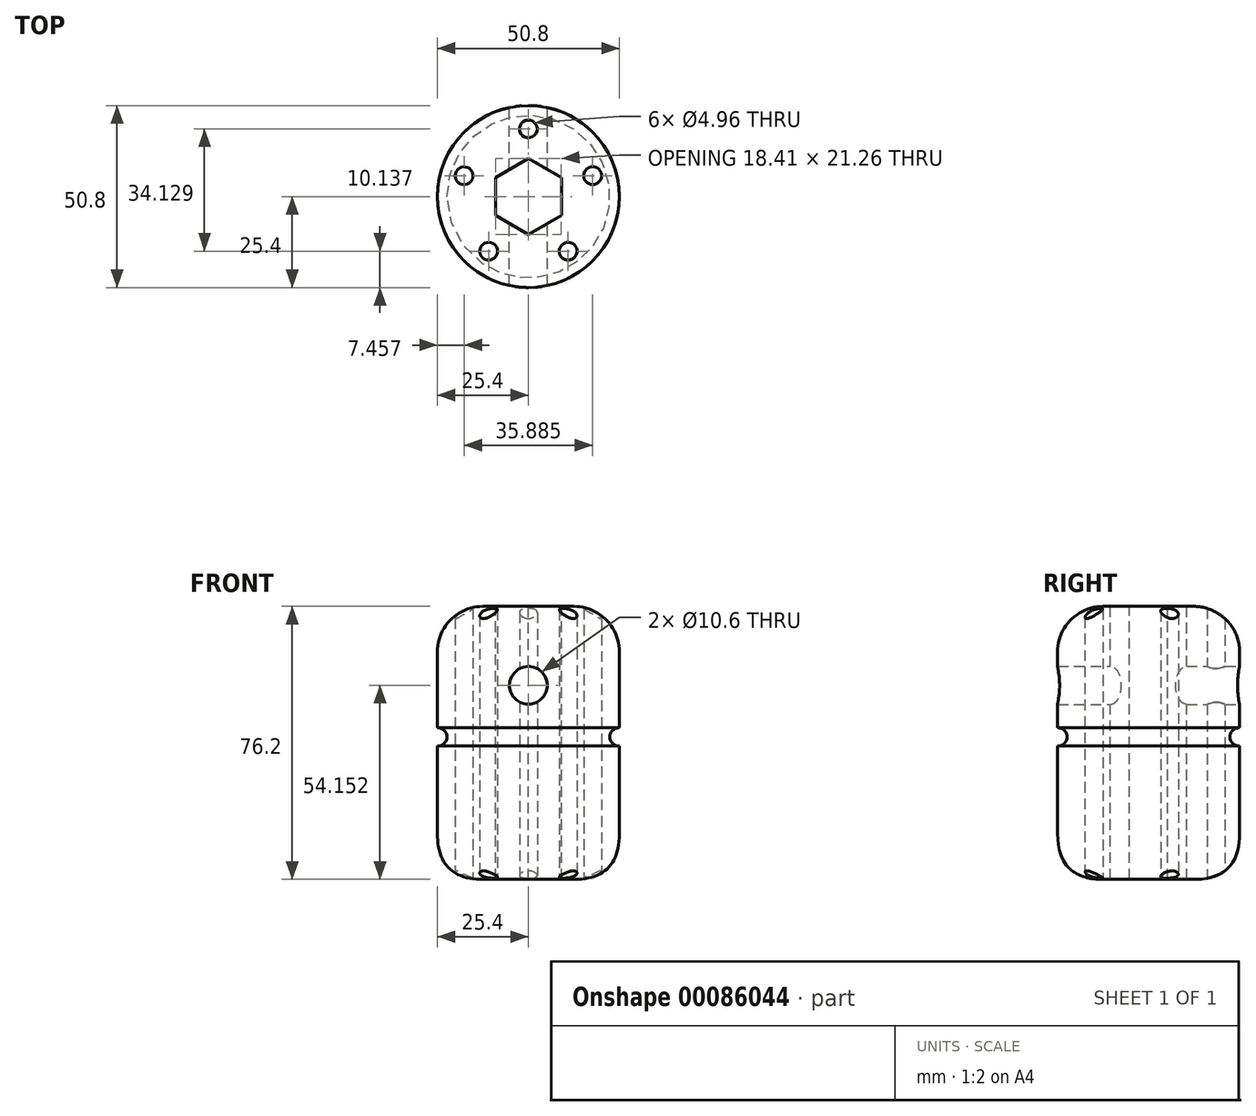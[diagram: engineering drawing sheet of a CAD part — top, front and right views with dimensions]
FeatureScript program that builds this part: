
annotation { "Feature Type Name" : "Feature", "Feature Type Description" : "" }
export const myFeature = defineFeature(function(context is Context, id is Id, definition is map)
    precondition{}
    {
        {
            var Q0;
            Q0=qCreatedBy(makeId("Top.planeOp"),FACE);
            var sketch = newSketch(context, id + "F0", { "sketchPlane" : qUnion([Q0])});
            skCircle(sketch, "E0", {"center": v(0, 0) * mm, "radius": 25.4 * mm});
            skSolve(sketch);
        }
        {
            var Q0;
            Q0 = qSketchRegion(id + "F0", true);
            extrude(context, id + "F1", {"entities" : qUnion([Q0]), "depth" : 76.2 * mm});
        }
        {
            var Q0;
            Q0=makeQuery(id+"F1.opExtrude","CAP_FACE",FACE,{"disambiguationData":[OSD([sQuery(id+"F0.wireOp",EDGE,"E0")])],"isStart":false});
            var sketch = newSketch(context, id + "F2", { "sketchPlane" : qUnion([Q0])});
            skCircle(sketch, "E1.cCircle", {"center": v(0, 0) * mm, "radius": 9.2 * mm, "construction": true});
            skLineSegment(sketch, "E1.0", {"start": v(9.2, 5.31) * mm, "end": v(9.2, -5.31) * mm});
            skLineSegment(sketch, "E1.1", {"start": v(9.2, -5.31) * mm, "end": v(0, -10.63) * mm});
            skLineSegment(sketch, "E1.2", {"start": v(0, -10.63) * mm, "end": v(-9.2, -5.31) * mm});
            skLineSegment(sketch, "E1.3", {"start": v(-9.2, -5.31) * mm, "end": v(-9.2, 5.31) * mm});
            skLineSegment(sketch, "E1.4", {"start": v(-9.2, 5.31) * mm, "end": v(0, 10.63) * mm});
            skLineSegment(sketch, "E1.5", {"start": v(0, 10.63) * mm, "end": v(9.2, 5.31) * mm});
            skPoint(sketch, "E1.0.midPoint", {"position": v(9.2, 0) * mm});
            skSolve(sketch);
        }
        {
            var Q0;
            Q0=makeQuery(id+"F2.imprint","IMPRINT",FACE,{"disambiguationData":[TD([[makeQuery(id+"F2.imprint","IMPRINT",EDGE,{"derivedFrom":sQuery(id+"F2.wireOp",EDGE,"E1.0")}),-1.0]])]});
            extrude(context, id + "F3", {"entities" : qUnion([Q0]), "operationType" : NewBodyOperationType.REMOVE, "oppositeDirection" : true, "depth" : 122.34 * mm});
        }
        {
            var Q0;
            Q0=makeQuery(id+"F1.opExtrude","CAP_EDGE",EDGE,{"disambiguationData":[OSD([sQuery(id+"F0.wireOp",EDGE,"E0")])],"isStart":false});
            fillet(context, id + "F4", {"entities" : qUnion([Q0]), "radius" : 12.7 * mm, "tangentPropagation" : true, "allowEdgeOverflow" : false});
        }
        {
            var Q0;
            Q0=makeQuery(id+"F1.opExtrude","CAP_EDGE",EDGE,{"disambiguationData":[OSD([sQuery(id+"F0.wireOp",EDGE,"E0")])],"isStart":true});
            fillet(context, id + "F5", {"entities" : qUnion([Q0]), "radius" : 12.7 * mm, "rho" : 0.5, "crossSection" : FilletCrossSection.CONIC, "allowEdgeOverflow" : false});
        }
        {
            var Q0;
            Q0=qCreatedBy(makeId("Front.planeOp"),FACE);
            var sketch = newSketch(context, id + "F6", { "sketchPlane" : qUnion([Q0])});
            skLineSegment(sketch, "E2", {"start": v(0, 84.63) * mm, "end": v(0, -19.1) * mm, "construction": true});
            skArc(sketch, "E3", {"start": v(-25.47, 37.24) * mm, "mid": v(-22.7, 39.77) * mm, "end": v(-25.47, 42.3) * mm});
            skLineSegment(sketch, "E4", {"start": v(-25.47, 42.3) * mm, "end": v(-25.47, 37.24) * mm});
            skSolve(sketch);
        }
        {
            var Q0;
            Q0 = qSketchRegion(id + "F6", true);
            var Q1;
            Q1=sQuery(id+"F6.wireOp",EDGE,"E2");
            revolve(context, id + "F7", {"operationType" : NewBodyOperationType.REMOVE, "entities" : qUnion([Q0]), "axis" : qUnion([Q1]), "revolveType" : RevolveType.FULL, "oppositeDirection" : true});
        }
        {
            var Q0;
            Q0=qCreatedBy(makeId("Front.planeOp"),FACE);
            var sketch = newSketch(context, id + "F8", { "sketchPlane" : qUnion([Q0])});
            skCircle(sketch, "E5", {"center": v(0, 54.15) * mm, "radius": 5.3 * mm});
            skSolve(sketch);
        }
        {
            var Q0;
            Q0 = qSketchRegion(id + "F8", true);
            extrude(context, id + "F9", {"entities" : qUnion([Q0]), "operationType" : NewBodyOperationType.REMOVE, "depth" : 25.4 * mm, "hasSecondDirection" : true, "secondDirectionOppositeDirection" : true, "secondDirectionDepth" : 25.4 * mm});
        }
        {
            var Q0;
            Q0=qCreatedBy(makeId("Top.planeOp"),FACE);
            var sketch = newSketch(context, id + "F10", { "sketchPlane" : qUnion([Q0])});
            skCircle(sketch, "E6", {"center": v(0, 18.87) * mm, "radius": 2.48 * mm});
            skCircle(sketch, "E7.1.0", {"center": v(-17.94, 5.83) * mm, "radius": 2.48 * mm});
            skCircle(sketch, "E7.2.0", {"center": v(-11.09, -15.26) * mm, "radius": 2.48 * mm});
            skCircle(sketch, "E7.3.0", {"center": v(11.09, -15.26) * mm, "radius": 2.48 * mm});
            skCircle(sketch, "E7.4.0", {"center": v(17.94, 5.83) * mm, "radius": 2.48 * mm});
            skPoint(sketch, "E7.center", {"position": v(0, 0) * mm});
            skSolve(sketch);
        }
        {
            var Q0;
            Q0 = qSketchRegion(id + "F10", true);
            extrude(context, id + "F11", {"entities" : qUnion([Q0]), "operationType" : NewBodyOperationType.REMOVE, "endBound" : BoundingType.THROUGH_ALL, "depth" : 25.4 * mm});
        }
    });
